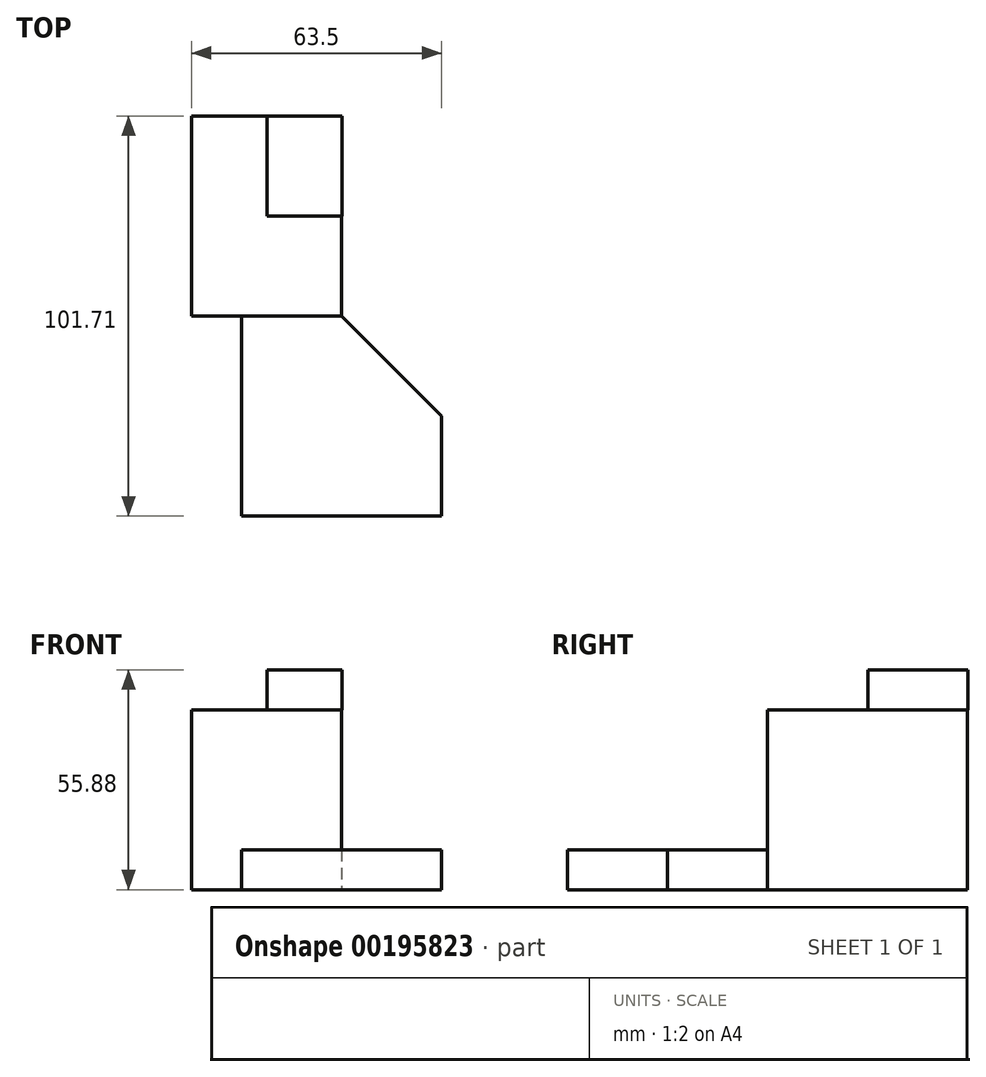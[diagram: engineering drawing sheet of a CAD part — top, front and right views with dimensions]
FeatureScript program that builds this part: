
annotation { "Feature Type Name" : "Feature", "Feature Type Description" : "" }
export const myFeature = defineFeature(function(context is Context, id is Id, definition is map)
    precondition{}
    {
        {
            var Q0;
            Q0=qCreatedBy(makeId("Top.planeOp"),FACE);
            var sketch = newSketch(context, id + "F0", { "sketchPlane" : qUnion([Q0])});
            skLineSegment(sketch, "E0.bottom", {"start": v(-44.44, 25.4) * mm, "end": v(-6.34, 25.4) * mm});
            skLineSegment(sketch, "E0.top", {"start": v(-44.44, -25.4) * mm, "end": v(-6.34, -25.4) * mm});
            skLineSegment(sketch, "E0.left", {"start": v(-44.44, 25.4) * mm, "end": v(-44.44, -25.4) * mm});
            skLineSegment(sketch, "E0.right", {"start": v(-6.34, 25.4) * mm, "end": v(-6.34, -25.4) * mm});
            skPoint(sketch, "E0.middle", {"position": v(-25.39, 0) * mm});
            skLineSegment(sketch, "E1.bottom", {"start": v(-31.74, -25.4) * mm, "end": v(19.06, -25.4) * mm});
            skLineSegment(sketch, "E1.top", {"start": v(-31.74, -76.2) * mm, "end": v(19.06, -76.2) * mm});
            skLineSegment(sketch, "E1.left", {"start": v(-31.74, -25.4) * mm, "end": v(-31.74, -76.2) * mm});
            skLineSegment(sketch, "E1.right", {"start": v(19.06, -25.4) * mm, "end": v(19.06, -76.2) * mm});
            skPoint(sketch, "E1.middle", {"position": v(-6.34, -50.8) * mm});
            skLineSegment(sketch, "E2", {"start": v(-6.34, -25.4) * mm, "end": v(19.06, -50.8) * mm});
            skSolve(sketch);
        }
        {
            var Q0;
            Q0=makeQuery(id+"F0.imprint","IMPRINT",FACE,{"disambiguationData":[TD([[makeQuery(id+"F0.imprint","IMPRINT",EDGE,{"derivedFrom":sQuery(id+"F0.wireOp",EDGE,"E0.bottom")}),-1.0]])]});
            extrude(context, id + "F1", {"entities" : qUnion([Q0]), "depth" : 45.72 * mm});
        }
        {
            var Q0;
            {var subQ1=sQuery(id+"F0.wireOp",EDGE,"E1.top");Q0=makeQuery(id+"F0.imprint","IMPRINT",FACE,{"disambiguationData":[TD([[makeQuery(id+"F0.imprint","IMPRINT",EDGE,{"derivedFrom":subQ1}),1.0]])]});}
            extrude(context, id + "F2", {"entities" : qUnion([Q0]), "operationType" : NewBodyOperationType.ADD, "depth" : 10.16 * mm});
        }
        {
            var Q0;
            Q0=qCreatedBy(makeId("Top.planeOp"),FACE);
            cPlane(context, id + "F3", {"entities" : qUnion([Q0]), "cplaneType" : CPlaneType.OFFSET, "offset" : 45.72 * mm, "width" : 152.4 * mm, "height" : 152.4 * mm});
        }
        {
            var Q0;
            Q0=qCreatedBy(id+"F3.planeOp",FACE);
            var sketch = newSketch(context, id + "F4", { "sketchPlane" : qUnion([Q0])});
            skLineSegment(sketch, "E3.bottom", {"start": v(-25.28, 25.51) * mm, "end": v(-6.23, 25.51) * mm});
            skLineSegment(sketch, "E3.top", {"start": v(-25.28, 0.11) * mm, "end": v(-6.23, 0.11) * mm});
            skLineSegment(sketch, "E3.left", {"start": v(-25.28, 25.51) * mm, "end": v(-25.28, 0.11) * mm});
            skLineSegment(sketch, "E3.right", {"start": v(-6.23, 25.51) * mm, "end": v(-6.23, 0.11) * mm});
            skPoint(sketch, "E3.middle", {"position": v(-15.76, 12.81) * mm});
            skSolve(sketch);
        }
        {
            var Q0;
            Q0=makeQuery(id+"F4.imprint","IMPRINT",FACE,{"disambiguationData":[TD([[makeQuery(id+"F4.imprint","IMPRINT",EDGE,{"derivedFrom":sQuery(id+"F4.wireOp",EDGE,"E3.bottom")}),-1.0]])]});
            extrude(context, id + "F5", {"entities" : qUnion([Q0]), "operationType" : NewBodyOperationType.ADD, "depth" : 10.16 * mm});
        }
    });
